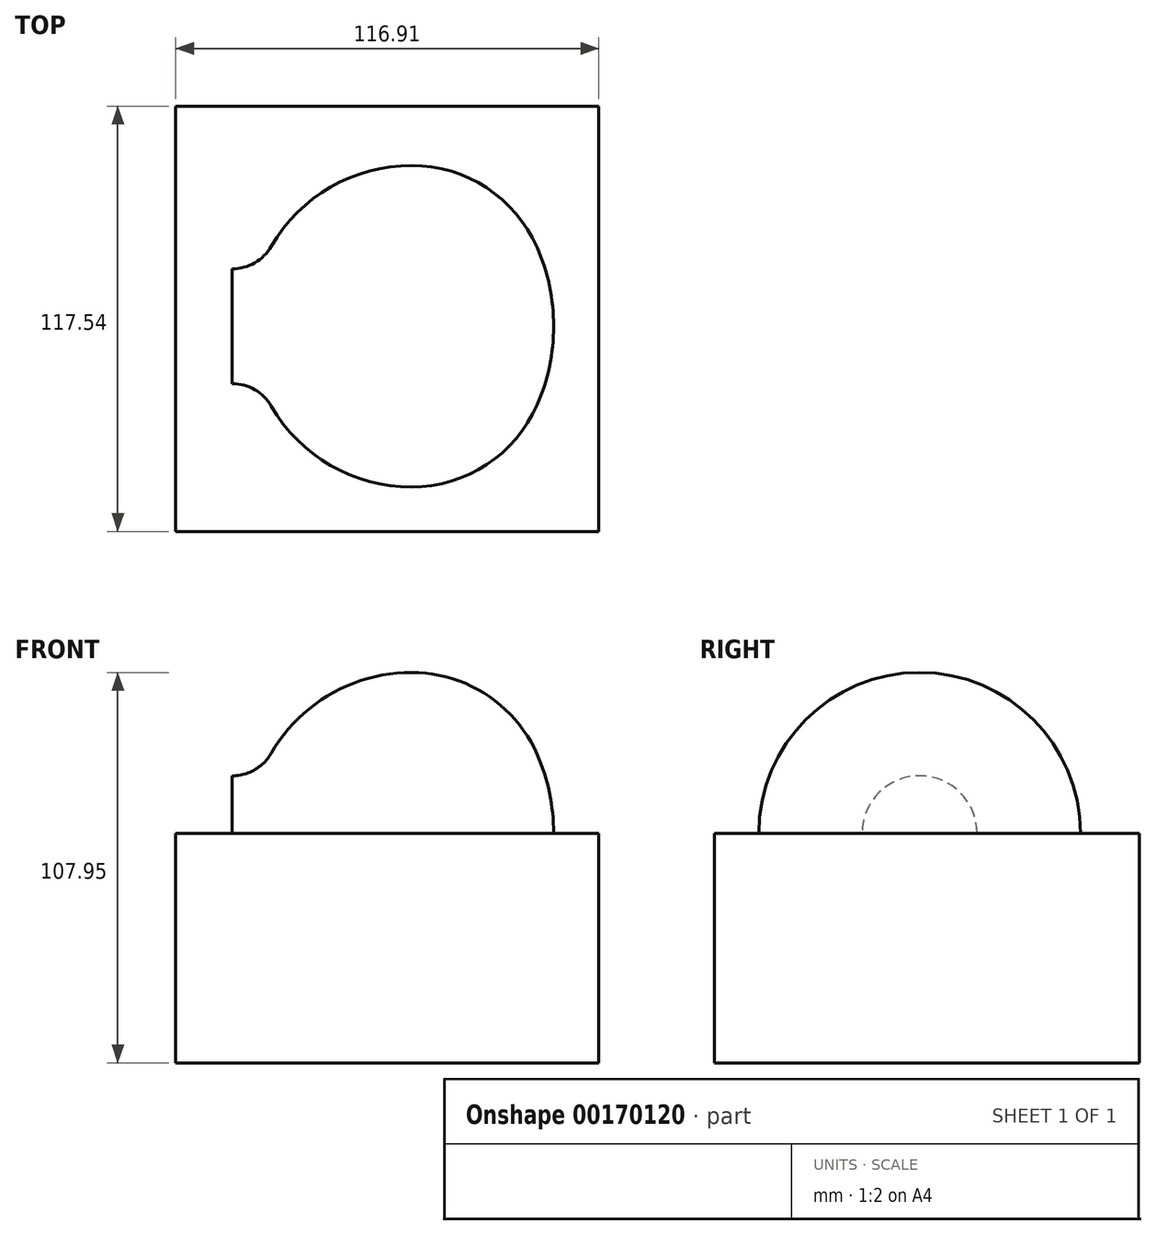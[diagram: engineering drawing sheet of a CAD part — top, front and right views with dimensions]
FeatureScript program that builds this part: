
annotation { "Feature Type Name" : "Feature", "Feature Type Description" : "" }
export const myFeature = defineFeature(function(context is Context, id is Id, definition is map)
    precondition{}
    {
        {
            var Q0;
            Q0=qCreatedBy(makeId("Top.planeOp"),FACE);
            var sketch = newSketch(context, id + "F0", { "sketchPlane" : qUnion([Q0])});
            skLineSegment(sketch, "E0", {"start": v(0, 0) * mm, "end": v(88.9, 0) * mm, "construction": true});
            skLineSegment(sketch, "E1", {"start": v(0, 0) * mm, "end": v(0, -15.88) * mm, "construction": true});
            skLineSegment(sketch, "E2", {"start": v(0, -15.88) * mm, "end": v(88.9, -15.88) * mm, "construction": true});
            skLineSegment(sketch, "E3", {"start": v(0, 0) * mm, "end": v(0, 28.58) * mm, "construction": true});
            skLineSegment(sketch, "E4", {"start": v(0, 28.58) * mm, "end": v(88.9, 28.58) * mm, "construction": true});
            skLineSegment(sketch, "E5", {"start": v(88.9, -15.88) * mm, "end": v(88.9, 28.58) * mm, "construction": true});
            skArc(sketch, "E6", {"start": v(88.9, -15.88) * mm, "mid": v(87.74, -4.74) * mm, "end": v(84.32, 5.91) * mm});
            skArc(sketch, "E7", {"start": v(84.32, 5.91) * mm, "mid": v(70.33, 22.4) * mm, "end": v(49.6, 28.58) * mm});
            skArc(sketch, "E8", {"start": v(0, 0) * mm, "mid": v(6.23, 1.67) * mm, "end": v(10.8, 6.22) * mm});
            skArc(sketch, "E9", {"start": v(49.6, 28.58) * mm, "mid": v(27.2, 22.59) * mm, "end": v(10.8, 6.22) * mm});
            skLineSegment(sketch, "E10", {"start": v(0, 0) * mm, "end": v(0, -15.88) * mm});
            skLineSegment(sketch, "E11", {"start": v(88.9, -15.88) * mm, "end": v(0, -15.88) * mm});
            skSolve(sketch);
        }
        {
            var Q0;
            Q0=makeQuery(id+"F0.imprint","IMPRINT",FACE,{"disambiguationData":[TD([[makeQuery(id+"F0.imprint","IMPRINT",EDGE,{"derivedFrom":sQuery(id+"F0.wireOp",EDGE,"E6")}),1.0]])]});
            var Q1;
            Q1=sQuery(id+"F0.wireOp",EDGE,"E11");
            revolve(context, id + "F1", {"entities" : qUnion([Q0]), "axis" : qUnion([Q1]), "revolveType" : RevolveType.FULL});
        }
        {
            var Q0;
            Q0=qCreatedBy(makeId("Top.planeOp"),FACE);
            var sketch = newSketch(context, id + "F2", { "sketchPlane" : qUnion([Q0])});
            skLineSegment(sketch, "E12.bottom", {"start": v(-15.57, 44.94) * mm, "end": v(101.34, 44.94) * mm});
            skLineSegment(sketch, "E12.top", {"start": v(-15.57, -72.6) * mm, "end": v(101.34, -72.6) * mm});
            skLineSegment(sketch, "E12.left", {"start": v(-15.57, 44.94) * mm, "end": v(-15.57, -72.6) * mm});
            skLineSegment(sketch, "E12.right", {"start": v(101.34, 44.94) * mm, "end": v(101.34, -72.6) * mm});
            skSolve(sketch);
        }
        {
            var Q0;
            Q0 = qSketchRegion(id + "F2", true);
            extrude(context, id + "F3", {"entities" : qUnion([Q0]), "operationType" : NewBodyOperationType.ADD, "oppositeDirection" : true, "depth" : 63.5 * mm});
        }
    });
